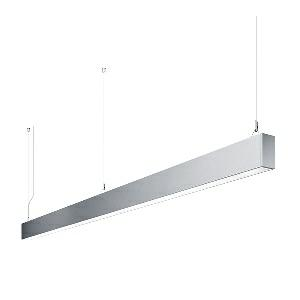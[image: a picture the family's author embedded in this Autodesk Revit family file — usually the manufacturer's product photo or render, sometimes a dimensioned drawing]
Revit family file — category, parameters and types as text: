
# Revit family: idoo_line_-_ilp_6000_840_d_00805678_eb2a
name_source: partatom
category: Lighting Fixtures
units: mm (PartAtom-declared; Revit-internal decimal feet)

## family parameters
Cut with Voids When Loaded = No
Host = Face
Light Source = No
Part Type = Normal
Room Calculation Point = No
Round Connector Dimension = Use Diameter
Shared = No

## types (1)
- IDOO.line - ILP 6000/840/D (1 x LED, 6300 lm, 4000K)
    Apparent Load = 46 VA
    Approval mark = CE
    CIE Flux Codes = 66 91 98 40 100
    Color Rendering = 80-89
    Color Temperature = 4000K
    Control Gear = Electronic ballast
    Default Elevation = 1800 mm
    Description = ILP 6000/840/D|Suspended luminaire|light source: LED|connected load: 220-240V, 50/60Hz|Power consumption: approx. 46 W|standby: approx. 0,15|luminous flux: 6300 lm|luminous efficacy: 136 lm/W|light distribution: Direct/indirect|direct ratio: approx. 40 %|colour temperature: Cold white, ca. 4000 K|color rendering index (CRI): >= 80|chromaticity tolerance:  3 SDCM|System of protection: IP 40|technology: Continuously dimmable|luminaire body|material: Sectional aluminium|colour: Silver|lamp cover: Acrylic (PMMA), Clear|mains lead: 2.00 m With free stranded wires|Fastening: Steel cable 0.3 - 0.7 m|glare control: Prism aperture|luminance(L65): <= 2700 cd/m|unified glare rating(4H 8H): <=  16|special features: DALI Load 1x, TouchDIM - dimming via standard switch, Flicker-free, Suitable as emergency lighting|
    Frequency = 50 Hz
    Height = 110 mm
    Lamp = 1 x LED
    Lamp Light Flux = 6300 lm
    Lamp count = 1
    Length = 2256 mm
    Luminous efficacy = 137 lm/W
    Manufacturer = Waldmann
    ModVariant = No
    Model = 00805678
    Mounting Place = Ceiling
    Mounting Type = Pendant
    Number of Poles = 1
    OnlyDefault = Yes
    Power Factor = 1
    Product Name = IDOO.line - ILP 6000/840/D
    Product group = Suspended luminaire
    ProductGroupID = 9
    Protection Class = Protection class I
    Protection Degree = IP 40
    RLX_Detail_Level = 1
    RLX_Emergency_Light_Flux = 0 lm
    RLX_Emergency_Type = 0
    RLX_Emergency_Type_DB = No
    RlxData = <blob elided: 23153 chars, md5=d1f8cad3>
    Socket = socket
    Standby Power = 0 W
    System Light Flux = 6300 lm
    System Power = 46 W
    Type Comments = Product without accessories
    Type Image = 113294000-00692533.jpg
    URL = http://relux.com
    VarID = ---
    Voltage = 230 V
    Voltage Range = 220-240 V
    Weight = 0.00 kg
    Width = 60 mm  [stored 0.19685 ft]

note: [stored X ft] marks values corroborated as IEEE doubles in the binary element streams (Revit-internal decimal feet)

## geometry (parser evidence)
native form markers: Blend x4, Sweep x15
no freeform markers — native parametric forms only
